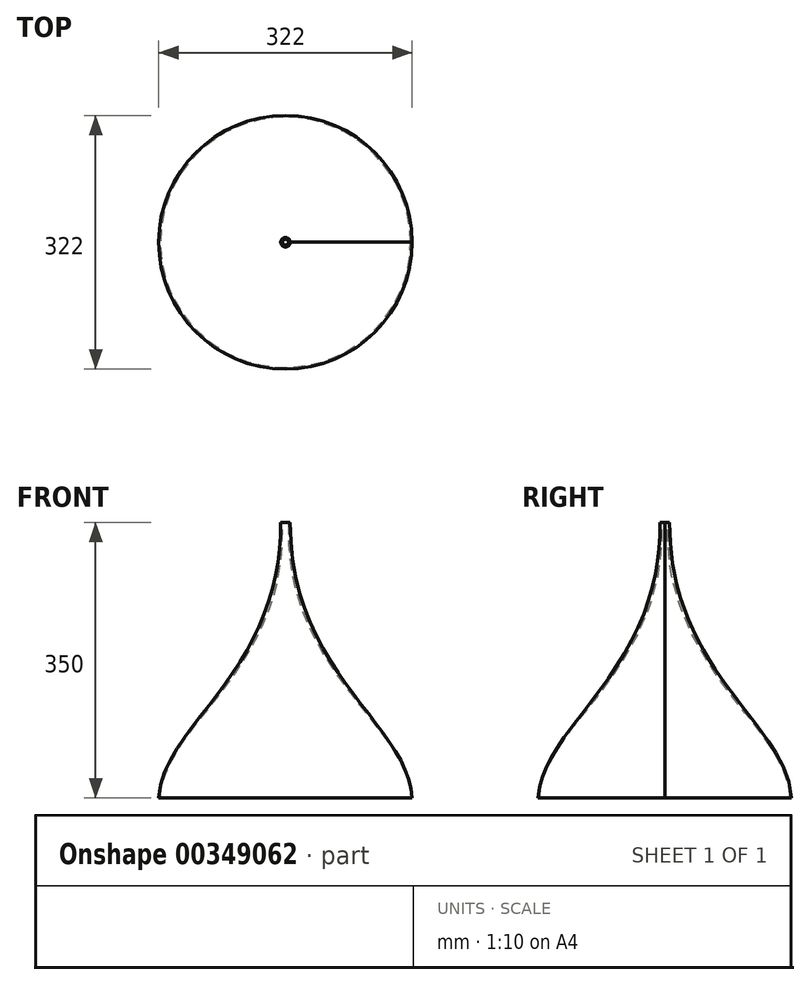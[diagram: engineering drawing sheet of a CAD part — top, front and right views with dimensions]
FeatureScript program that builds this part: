
annotation { "Feature Type Name" : "Feature", "Feature Type Description" : "" }
export const myFeature = defineFeature(function(context is Context, id is Id, definition is map)
    precondition{}
    {
        {
            var Q0;
            Q0=qCreatedBy(makeId("Front.planeOp"),FACE);
            var sketch = newSketch(context, id + "F0", { "sketchPlane" : qUnion([Q0])});
            skFitSpline(sketch, "E0", {"points": [v(-6, 38.38) * mm, v(-161, -311.62) * mm], "startDerivative": vector(0, -575.13) * mm, "endDerivative": vector(-17, -285.04) * mm});
            skFitSpline(sketch, "E1.0", {"points": [v(-4, 38.38) * mm, v(-4, 14.29) * mm, v(-8.7, -29.9) * mm, v(-26.38, -85.98) * mm, v(-51.22, -133.67) * mm, v(-79.73, -174.84) * mm, v(-108.43, -211.36) * mm, v(-129.6, -239.46) * mm, v(-143.2, -261.44) * mm, v(-151.28, -277.9) * mm, v(-156.87, -294.54) * mm, v(-158.66, -305.93) * mm, v(-159, -311.74) * mm]});
            skLineSegment(sketch, "E2", {"start": v(-6, 38.38) * mm, "end": v(-4, 38.38) * mm});
            skLineSegment(sketch, "E3", {"start": v(-161, -311.62) * mm, "end": v(-159, -311.62) * mm});
            skSolve(sketch);
        }
        {
            var Q0;
            Q0=qCreatedBy(makeId("Front.planeOp"),FACE);
            var sketch = newSketch(context, id + "F1", { "sketchPlane" : qUnion([Q0])});
            skLineSegment(sketch, "E4", {"start": v(0, 65.53) * mm, "end": v(0, -62.94) * mm});
            skSolve(sketch);
        }
        {
            var Q0;
            Q0=qSketchRegion(id+"F0",true);
            var Q1;
            Q1=sQuery(id+"F1.wireOp",EDGE,"E4");
            revolve(context, id + "F2", {"entities" : qUnion([Q0]), "axis" : qUnion([Q1]), "revolveType" : RevolveType.FULL});
        }
    });
